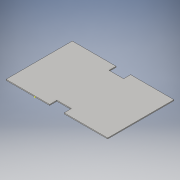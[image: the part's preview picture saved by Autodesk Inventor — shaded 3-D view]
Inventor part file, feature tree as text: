
AUTODESK INVENTOR PART (.ipt)
format: ipt  version: 2016 (Build 200138000, 138)  size: 109,056 bytes
history: native  units: in
note: dims shown in document units (in); Inventor stores cm internally (conversion verified against a paired STEP export)
features: sketch x4, extrude x2
ambient origin geometry x8: Origin, YZ Plane, XZ Plane, XY Plane, X Axis, Y Axis, Z Axis, Center Point
bodies: Solid1 (feature_tree)
feature tree (6):
  sketch  "Sketch1"  dims[d0=18.25in d1=28.0in]
  extrude  "Extrusion1"  Depth=28.0in
  extrude  "Extrusion2"  Depth=2.0in
  sketch  "Sketch4"  dims[d6=12.0in d8=2.0in d9=4.0in d10=0.0in d11=0.25in d12=0.0in]
  sketch  "Sketch2"  dims[d2=0.25in d3=0.0in d4=2.0in]
  sketch  "Sketch3"  dims[d5=4.0in]
